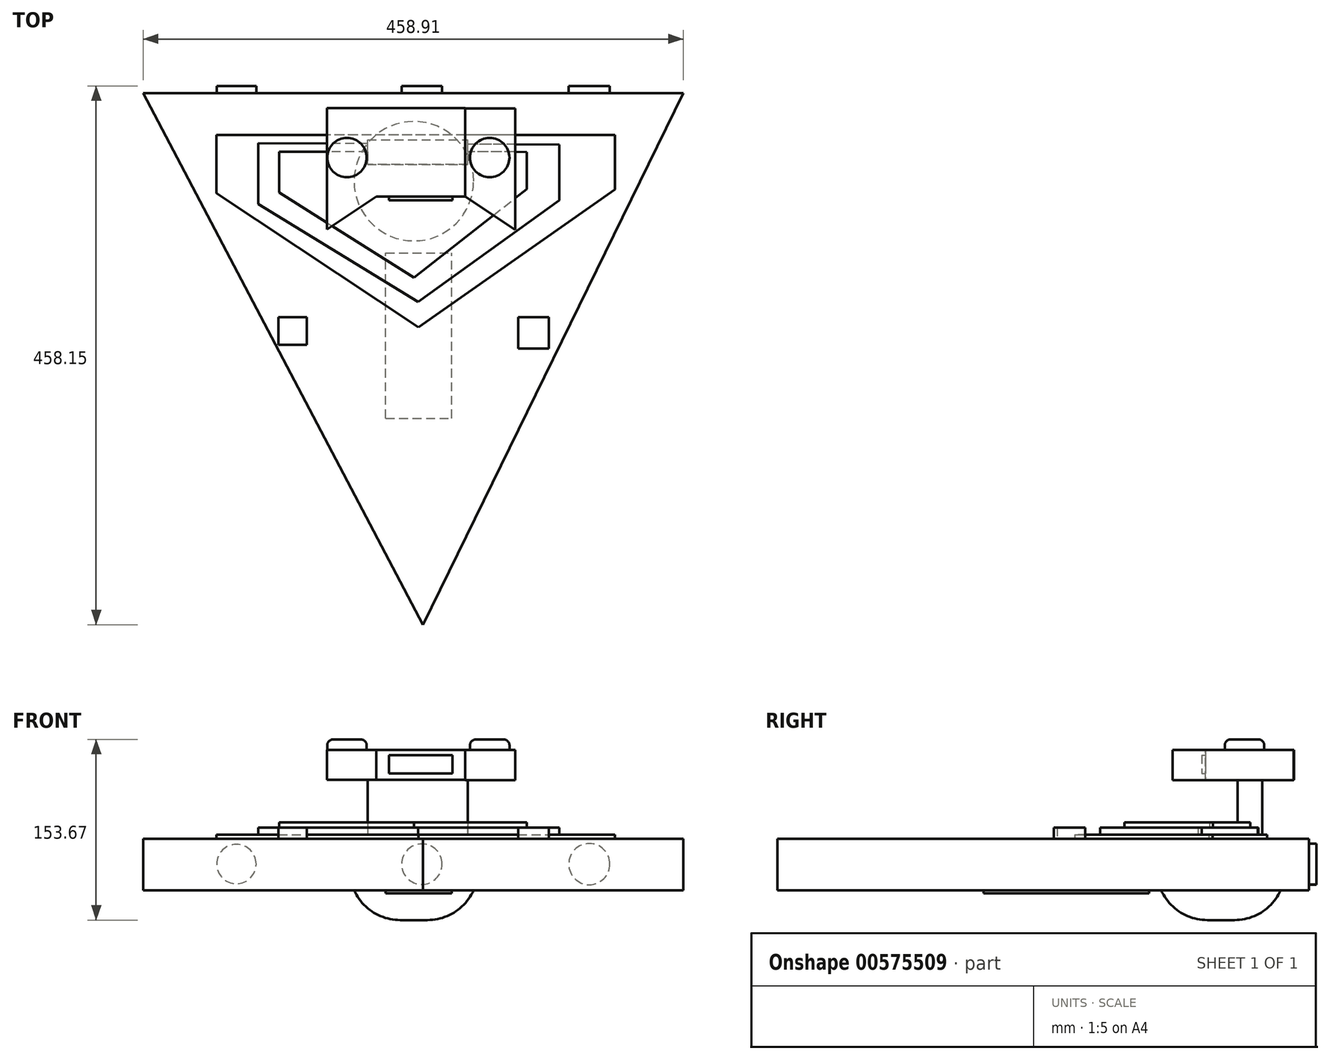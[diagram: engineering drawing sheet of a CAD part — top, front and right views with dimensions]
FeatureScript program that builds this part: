
annotation { "Feature Type Name" : "Feature", "Feature Type Description" : "" }
export const myFeature = defineFeature(function(context is Context, id is Id, definition is map)
    precondition{}
    {
        {
            var Q0;
            Q0=qCreatedBy(makeId("Top.planeOp"),FACE);
            var sketch = newSketch(context, id + "F0", { "sketchPlane" : qUnion([Q0])});
            skLineSegment(sketch, "E0.bottom", {"start": v(0, 0) * mm, "end": v(75.39, 0) * mm});
            skLineSegment(sketch, "E0.top", {"start": v(0, -75.18) * mm, "end": v(75.39, -75.18) * mm});
            skLineSegment(sketch, "E0.left", {"start": v(0, 0) * mm, "end": v(0, -75.18) * mm});
            skLineSegment(sketch, "E0.right", {"start": v(75.39, 0) * mm, "end": v(75.39, -75.18) * mm});
            skSolve(sketch);
        }
        {
            var Q0;
            Q0 = qSketchRegion(id + "F0", true);
            extrude(context, id + "F1", {"entities" : qUnion([Q0]), "depth" : 25.4 * mm, "offsetDistance" : 25.4 * mm});
        }
        {
            var Q0;
            Q0=makeQuery(id+"F1.opExtrude","CAP_FACE",FACE,{"disambiguationData":[OSD([sQuery(id+"F0.wireOp",EDGE,"E0.bottom"),sQuery(id+"F0.wireOp",EDGE,"E0.top"),sQuery(id+"F0.wireOp",EDGE,"E0.left"),sQuery(id+"F0.wireOp",EDGE,"E0.right")])],"isStart":false});
            var sketch = newSketch(context, id + "F2", { "sketchPlane" : qUnion([Q0])});
            skLineSegment(sketch, "E1", {"start": v(0, 0) * mm, "end": v(-42.02, 0) * mm});
            skLineSegment(sketch, "E2", {"start": v(-42.02, 0) * mm, "end": v(-42.02, -103.17) * mm});
            skLineSegment(sketch, "E3", {"start": v(-42.02, -103.17) * mm, "end": v(0, -75.18) * mm});
            skLineSegment(sketch, "E4", {"start": v(0, -75.18) * mm, "end": v(0, 0) * mm});
            skSolve(sketch);
        }
        {
            var Q0;
            Q0=makeQuery(id+"F2.imprint","IMPRINT",FACE,{"disambiguationData":[TD([[makeQuery(id+"F2.imprint","IMPRINT",EDGE,{"derivedFrom":sQuery(id+"F2.wireOp",EDGE,"E4")}),1.0]])]});
            var sketch = newSketch(context, id + "F3", { "sketchPlane" : qUnion([Q0])});
            skLineSegment(sketch, "E5", {"start": v(75.76, -0.25) * mm, "end": v(118.1, -0.25) * mm});
            skLineSegment(sketch, "E6", {"start": v(118.1, -0.25) * mm, "end": v(118.1, -103.26) * mm});
            skLineSegment(sketch, "E7", {"start": v(118.1, -103.26) * mm, "end": v(75.4, -75.18) * mm});
            skLineSegment(sketch, "E8", {"start": v(75.4, -75.18) * mm, "end": v(75.4, -0.25) * mm});
            skLineSegment(sketch, "E9", {"start": v(75.4, -0.25) * mm, "end": v(75.76, -0.25) * mm});
            skSolve(sketch);
        }
        {
            var Q0;
            Q0 = qSketchRegion(id + "F2", true);
            extrude(context, id + "F4", {"entities" : qUnion([Q0]), "operationType" : NewBodyOperationType.ADD, "oppositeDirection" : true, "depth" : 25.4 * mm, "offsetDistance" : 25.4 * mm});
        }
        {
            var Q0;
            Q0 = qSketchRegion(id + "F3", true);
            extrude(context, id + "F5", {"entities" : qUnion([Q0]), "oppositeDirection" : true, "depth" : 25.45 * mm, "offsetDistance" : 25.4 * mm});
        }
        {
            var Q0;
            Q0=makeQuery(id+"F1.opExtrude","SWEPT_FACE",FACE,{"disambiguationData":[OSD([sQuery(id+"F0.wireOp",EDGE,"E0.top")])]});
            var sketch = newSketch(context, id + "F6", { "sketchPlane" : qUnion([Q0])});
            skLineSegment(sketch, "E10.bottom", {"start": v(10.6, 21.13) * mm, "end": v(64.53, 21.13) * mm});
            skLineSegment(sketch, "E10.top", {"start": v(10.6, 5.43) * mm, "end": v(64.53, 5.43) * mm});
            skLineSegment(sketch, "E10.left", {"start": v(10.6, 21.13) * mm, "end": v(10.6, 5.43) * mm});
            skLineSegment(sketch, "E10.right", {"start": v(64.53, 21.13) * mm, "end": v(64.53, 5.43) * mm});
            skSolve(sketch);
        }
        {
            var Q0;
            Q0 = qSketchRegion(id + "F6", true);
            extrude(context, id + "F7", {"entities" : qUnion([Q0]), "depth" : 3.05 * mm, "offsetDistance" : 25.4 * mm});
        }
        {
            var Q0;
            Q0=makeQuery(id+"F4.boolean.opBoolean","MERGE",FACE,{"derivedFrom":[makeQuery(id+"F1.opExtrude","CAP_FACE",FACE,{"disambiguationData":[OSD([sQuery(id+"F0.wireOp",EDGE,"E0.bottom"),sQuery(id+"F0.wireOp",EDGE,"E0.top"),sQuery(id+"F0.wireOp",EDGE,"E0.left"),sQuery(id+"F0.wireOp",EDGE,"E0.right")])],"isStart":true}),makeQuery(id+"F4.opExtrude","CAP_FACE",FACE,{"disambiguationData":[OSD([sQuery(id+"F2.wireOp",EDGE,"E1"),sQuery(id+"F2.wireOp",EDGE,"E2"),sQuery(id+"F2.wireOp",EDGE,"E3"),sQuery(id+"F2.wireOp",EDGE,"E4")])],"isStart":false})]});
            var sketch = newSketch(context, id + "F8", { "sketchPlane" : qUnion([Q0])});
            skLineSegment(sketch, "E11.bottom", {"start": v(-7.48, 47.96) * mm, "end": v(77.7, 47.96) * mm});
            skLineSegment(sketch, "E11.top", {"start": v(-7.48, 27.03) * mm, "end": v(77.7, 27.03) * mm});
            skLineSegment(sketch, "E11.left", {"start": v(-7.48, 47.96) * mm, "end": v(-7.48, 27.03) * mm});
            skLineSegment(sketch, "E11.right", {"start": v(77.7, 47.96) * mm, "end": v(77.7, 27.03) * mm});
            skSolve(sketch);
        }
        {
            var Q0;
            Q0 = qSketchRegion(id + "F8", true);
            extrude(context, id + "F9", {"entities" : qUnion([Q0]), "depth" : 50.04 * mm, "offsetDistance" : 25.4 * mm});
        }
        {
            var Q0;
            Q0=makeQuery(id+"F9.opExtrude","CAP_FACE",FACE,{"disambiguationData":[OSD([sQuery(id+"F8.wireOp",EDGE,"E11.bottom"),sQuery(id+"F8.wireOp",EDGE,"E11.top"),sQuery(id+"F8.wireOp",EDGE,"E11.left"),sQuery(id+"F8.wireOp",EDGE,"E11.right")])],"isStart":false});
            var sketch = newSketch(context, id + "F10", { "sketchPlane" : qUnion([Q0])});
            skLineSegment(sketch, "E12", {"start": v(39.48, 35.16) * mm, "end": v(39.48, 439.17) * mm});
            skLineSegment(sketch, "E13", {"start": v(39.48, 439.17) * mm, "end": v(260.77, -12.88) * mm});
            skLineSegment(sketch, "E14", {"start": v(260.77, -12.88) * mm, "end": v(-198.14, -12.88) * mm});
            skLineSegment(sketch, "E15", {"start": v(-198.14, -12.88) * mm, "end": v(39.48, 439.17) * mm});
            skSolve(sketch);
        }
        {
            var Q0;
            Q0 = qSketchRegion(id + "F10", true);
            extrude(context, id + "F11", {"entities" : qUnion([Q0]), "operationType" : NewBodyOperationType.ADD, "depth" : 43.69 * mm, "offsetDistance" : 25.4 * mm});
        }
        {
            var Q0;
            Q0=makeQuery(id+"F11.opExtrude","SWEPT_FACE",FACE,{"disambiguationData":[OSD([sQuery(id+"F10.wireOp",EDGE,"E14")])]});
            var sketch = newSketch(context, id + "F12", { "sketchPlane" : qUnion([Q0])});
            skCircle(sketch, "E16", {"center": v(-38.64, -71.55) * mm, "radius": 17.2 * mm});
            skCircle(sketch, "E17", {"center": v(-180.98, -71.55) * mm, "radius": 17.5 * mm});
            skCircle(sketch, "E18", {"center": v(118.97, -71.55) * mm, "radius": 16.77 * mm});
            skSolve(sketch);
        }
        {
            var Q0;
            Q0 = qSketchRegion(id + "F12", true);
            extrude(context, id + "F13", {"entities" : qUnion([Q0]), "depth" : 6.1 * mm, "offsetDistance" : 25.4 * mm});
        }
        {
            var Q0;
            Q0=makeQuery(id+"F10.imprint","IMPRINT",FACE,{"disambiguationData":[TD([[makeQuery(id+"F10.imprint","IMPRINT",EDGE,{"derivedFrom":sQuery(id+"F10.wireOp",EDGE,"E13")}),-1.0]])]});
            var sketch = newSketch(context, id + "F14", { "sketchPlane" : qUnion([Q0])});
            skLineSegment(sketch, "E19", {"start": v(-135.85, 31.48) * mm, "end": v(-135.85, 72.34) * mm});
            skLineSegment(sketch, "E20", {"start": v(-135.85, 72.34) * mm, "end": v(35.65, 186.26) * mm});
            skLineSegment(sketch, "E21", {"start": v(35.65, 186.26) * mm, "end": v(202.81, 69.25) * mm});
            skLineSegment(sketch, "E22", {"start": v(202.81, 69.25) * mm, "end": v(202.81, 22.81) * mm});
            skLineSegment(sketch, "E23", {"start": v(202.81, 22.81) * mm, "end": v(-135.85, 22.81) * mm});
            skLineSegment(sketch, "E24", {"start": v(-135.85, 22.81) * mm, "end": v(-135.85, 31.48) * mm});
            skSolve(sketch);
        }
        {
            var Q0;
            Q0 = qSketchRegion(id + "F14", true);
            extrude(context, id + "F15", {"entities" : qUnion([Q0]), "operationType" : NewBodyOperationType.ADD, "oppositeDirection" : true, "depth" : 3.56 * mm, "offsetDistance" : 25.4 * mm});
        }
        {
            var Q0;
            Q0=makeQuery(id+"F15.opExtrude","CAP_FACE",FACE,{"disambiguationData":[OSD([sQuery(id+"F14.wireOp",EDGE,"E19"),sQuery(id+"F14.wireOp",EDGE,"E20"),sQuery(id+"F14.wireOp",EDGE,"E21"),sQuery(id+"F14.wireOp",EDGE,"E22"),sQuery(id+"F14.wireOp",EDGE,"E23"),sQuery(id+"F14.wireOp",EDGE,"E24")])],"isStart":false});
            var sketch = newSketch(context, id + "F16", { "sketchPlane" : qUnion([Q0])});
            skLineSegment(sketch, "E25", {"start": v(-100.56, -29.7) * mm, "end": v(-100.56, -81.44) * mm});
            skLineSegment(sketch, "E26", {"start": v(-100.56, -81.44) * mm, "end": v(35.44, -164.78) * mm});
            skLineSegment(sketch, "E27", {"start": v(35.44, -164.78) * mm, "end": v(155.4, -78.34) * mm});
            skLineSegment(sketch, "E28", {"start": v(155.4, -78.34) * mm, "end": v(155.4, -30.92) * mm});
            skLineSegment(sketch, "E29", {"start": v(155.4, -30.92) * mm, "end": v(-100.56, -29.7) * mm});
            skSolve(sketch);
        }
        {
            var Q0;
            {var subQ6=sQuery(id+"F16.wireOp",EDGE,"E25");Q0=makeQuery(id+"F16.imprint","IMPRINT",FACE,{"disambiguationData":[TD([[makeQuery(id+"F16.imprint","IMPRINT",EDGE,{"derivedFrom":subQ6}),1.0]])]});}
            extrude(context, id + "F17", {"entities" : qUnion([Q0]), "operationType" : NewBodyOperationType.ADD, "depth" : 6.1 * mm, "offsetDistance" : 25.4 * mm});
        }
        {
            var Q0;
            Q0=makeQuery(id+"F11.opExtrude","CAP_FACE",FACE,{"disambiguationData":[OSD([sQuery(id+"F10.wireOp",EDGE,"E13"),sQuery(id+"F10.wireOp",EDGE,"E14"),sQuery(id+"F10.wireOp",EDGE,"E15")])],"isStart":true});
            var sketch = newSketch(context, id + "F18", { "sketchPlane" : qUnion([Q0])});
            skLineSegment(sketch, "E30.bottom", {"start": v(-83.22, -177.6) * mm, "end": v(-59.08, -177.6) * mm});
            skLineSegment(sketch, "E30.top", {"start": v(-83.22, -201.12) * mm, "end": v(-59.08, -201.12) * mm});
            skLineSegment(sketch, "E30.left", {"start": v(-83.22, -177.6) * mm, "end": v(-83.22, -201.12) * mm});
            skLineSegment(sketch, "E30.right", {"start": v(-59.08, -177.6) * mm, "end": v(-59.08, -201.12) * mm});
            skLineSegment(sketch, "E31.bottom", {"start": v(120.47, -177.6) * mm, "end": v(146.47, -177.6) * mm});
            skLineSegment(sketch, "E31.top", {"start": v(120.47, -204.22) * mm, "end": v(146.47, -204.22) * mm});
            skLineSegment(sketch, "E31.left", {"start": v(120.47, -177.6) * mm, "end": v(120.47, -204.22) * mm});
            skLineSegment(sketch, "E31.right", {"start": v(146.47, -177.6) * mm, "end": v(146.47, -204.22) * mm});
            skSolve(sketch);
        }
        {
            var Q0;
            Q0 = qSketchRegion(id + "F18", true);
            extrude(context, id + "F19", {"entities" : qUnion([Q0]), "operationType" : NewBodyOperationType.ADD, "depth" : 9.65 * mm, "offsetDistance" : 25.4 * mm});
        }
        {
            var Q0;
            Q0=makeQuery(id+"F11.opExtrude","CAP_FACE",FACE,{"disambiguationData":[OSD([sQuery(id+"F10.wireOp",EDGE,"E13"),sQuery(id+"F10.wireOp",EDGE,"E14"),sQuery(id+"F10.wireOp",EDGE,"E15")])],"isStart":false});
            var sketch = newSketch(context, id + "F20", { "sketchPlane" : qUnion([Q0])});
            skLineSegment(sketch, "E32.bottom", {"start": v(7.79, 263.65) * mm, "end": v(64.13, 263.65) * mm});
            skLineSegment(sketch, "E32.top", {"start": v(7.79, 123.1) * mm, "end": v(64.13, 123.1) * mm});
            skLineSegment(sketch, "E32.left", {"start": v(7.79, 263.65) * mm, "end": v(7.79, 123.1) * mm});
            skLineSegment(sketch, "E32.right", {"start": v(64.13, 263.65) * mm, "end": v(64.13, 123.1) * mm});
            skSolve(sketch);
        }
        {
            var Q0;
            Q0 = qSketchRegion(id + "F20", true);
            extrude(context, id + "F21", {"entities" : qUnion([Q0]), "depth" : 2.54 * mm, "offsetDistance" : 25.4 * mm});
        }
        {
            var Q0;
            Q0=makeQuery(id+"F17.opExtrude","CAP_FACE",FACE,{"disambiguationData":[OSD([sQuery(id+"F8.wireOp",EDGE,"E11.bottom"),sQuery(id+"F8.wireOp",EDGE,"E11.left"),sQuery(id+"F8.wireOp",EDGE,"E11.right"),sQuery(id+"F14.wireOp",EDGE,"E19"),sQuery(id+"F14.wireOp",EDGE,"E20"),sQuery(id+"F14.wireOp",EDGE,"E21"),sQuery(id+"F14.wireOp",EDGE,"E22"),sQuery(id+"F14.wireOp",EDGE,"E23"),sQuery(id+"F14.wireOp",EDGE,"E24"),sQuery(id+"F16.wireOp",EDGE,"E25"),sQuery(id+"F16.wireOp",EDGE,"E26"),sQuery(id+"F16.wireOp",EDGE,"E27"),sQuery(id+"F16.wireOp",EDGE,"E28"),sQuery(id+"F16.wireOp",EDGE,"E29")])],"isStart":false});
            var sketch = newSketch(context, id + "F22", { "sketchPlane" : qUnion([Q0])});
            skLineSegment(sketch, "E33", {"start": v(-82.53, -37.08) * mm, "end": v(-82.53, -71.57) * mm});
            skLineSegment(sketch, "E34", {"start": v(-82.53, -71.57) * mm, "end": v(31.83, -144.1) * mm});
            skLineSegment(sketch, "E35", {"start": v(31.83, -144.1) * mm, "end": v(127.81, -68.71) * mm});
            skLineSegment(sketch, "E36", {"start": v(127.81, -68.71) * mm, "end": v(127.81, -37.21) * mm});
            skLineSegment(sketch, "E37", {"start": v(127.81, -37.21) * mm, "end": v(-82.53, -37.08) * mm});
            skSolve(sketch);
        }
        {
            var Q0;
            Q0 = qSketchRegion(id + "F22", true);
            extrude(context, id + "F23", {"entities" : qUnion([Q0]), "operationType" : NewBodyOperationType.ADD, "depth" : 4.32 * mm, "offsetDistance" : 25.4 * mm});
        }
        {
            var Q0;
            Q0=makeQuery(id+"F4.boolean.opBoolean","MERGE",FACE,{"derivedFrom":[makeQuery(id+"F1.opExtrude","CAP_FACE",FACE,{"disambiguationData":[OSD([sQuery(id+"F0.wireOp",EDGE,"E0.bottom"),sQuery(id+"F0.wireOp",EDGE,"E0.top"),sQuery(id+"F0.wireOp",EDGE,"E0.left"),sQuery(id+"F0.wireOp",EDGE,"E0.right")])],"isStart":false}),makeQuery(id+"F4.opExtrude","CAP_FACE",FACE,{"disambiguationData":[OSD([sQuery(id+"F2.wireOp",EDGE,"E1"),sQuery(id+"F2.wireOp",EDGE,"E2"),sQuery(id+"F2.wireOp",EDGE,"E3"),sQuery(id+"F2.wireOp",EDGE,"E4")])],"isStart":true})]});
            var sketch = newSketch(context, id + "F24", { "sketchPlane" : qUnion([Q0])});
            skCircle(sketch, "E38", {"center": v(-25.03, -42) * mm, "radius": 16.72 * mm});
            skCircle(sketch, "E39", {"center": v(96.32, -42) * mm, "radius": 16.76 * mm});
            skSolve(sketch);
        }
        {
            var Q0;
            Q0 = qSketchRegion(id + "F24", true);
            extrude(context, id + "F25", {"entities" : qUnion([Q0]), "depth" : 9.14 * mm, "offsetDistance" : 25.4 * mm});
        }
        {
            var Q0;
            Q0=makeQuery(id+"F25.opExtrude","CAP_EDGE",EDGE,{"disambiguationData":[OSD([sQuery(id+"F24.wireOp",EDGE,"E38")])],"isStart":false});
            var Q1;
            Q1=makeQuery(id+"F25.opExtrude","CAP_EDGE",EDGE,{"disambiguationData":[OSD([sQuery(id+"F24.wireOp",EDGE,"E39")])],"isStart":false});
            fillet(context, id + "F26", {"entities" : qUnion([Q0, Q1]), "radius" : 5.08 * mm, "tangentPropagation" : true, "allowEdgeOverflow" : false});
        }
        {
            var Q0;
            Q0=makeQuery(id+"F11.opExtrude","CAP_FACE",FACE,{"disambiguationData":[OSD([sQuery(id+"F10.wireOp",EDGE,"E13"),sQuery(id+"F10.wireOp",EDGE,"E14"),sQuery(id+"F10.wireOp",EDGE,"E15")])],"isStart":false});
            var sketch = newSketch(context, id + "F27", { "sketchPlane" : qUnion([Q0])});
            skCircle(sketch, "E40", {"center": v(31.83, 62.08) * mm, "radius": 50.77 * mm});
            skSolve(sketch);
        }
        {
            var Q0;
            Q0 = qSketchRegion(id + "F27", true);
            extrude(context, id + "F28", {"entities" : qUnion([Q0]), "operationType" : NewBodyOperationType.ADD, "depth" : 25.4 * mm, "offsetDistance" : 25.4 * mm});
        }
        {
            var Q0;
            Q0=makeQuery(id+"F28.opExtrude","CAP_EDGE",EDGE,{"disambiguationData":[OSD([sQuery(id+"F27.wireOp",EDGE,"E40")])],"isStart":false});
            fillet(context, id + "F29", {"entities" : qUnion([Q0]), "radius" : 42.92 * mm, "tangentPropagation" : true, "allowEdgeOverflow" : false});
        }
    });
